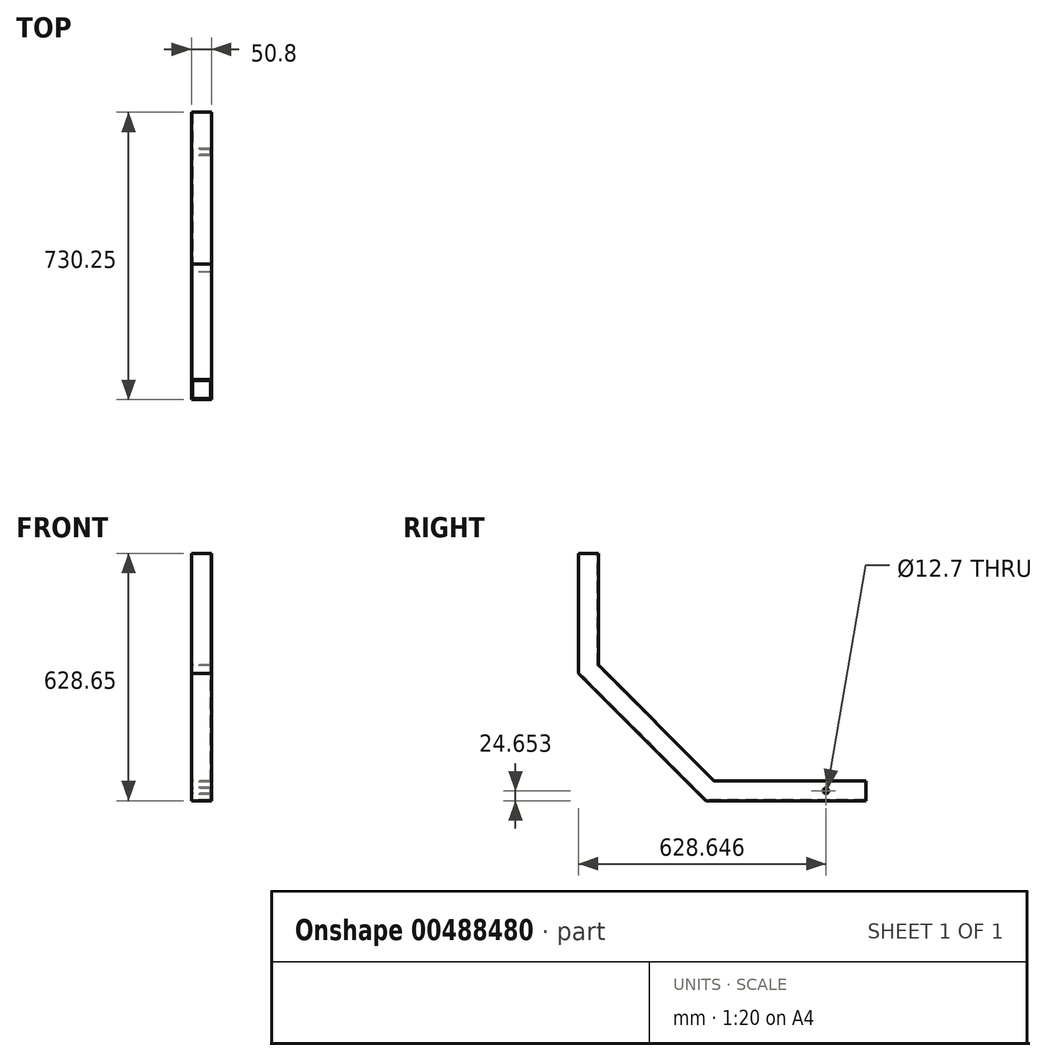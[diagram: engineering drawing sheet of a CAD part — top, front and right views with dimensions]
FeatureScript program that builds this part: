
annotation { "Feature Type Name" : "Feature", "Feature Type Description" : "" }
export const myFeature = defineFeature(function(context is Context, id is Id, definition is map)
    precondition{}
    {
        {
            var Q0;
            Q0=qCreatedBy(makeId("Right.planeOp"),FACE);
            var sketch = newSketch(context, id + "F0", { "sketchPlane" : qUnion([Q0])});
            skLineSegment(sketch, "E0", {"start": v(223.09, -341.59) * mm, "end": v(-183.31, -341.59) * mm});
            skLineSegment(sketch, "E1", {"start": v(-183.31, -341.59) * mm, "end": v(-507.16, -17.74) * mm});
            skLineSegment(sketch, "E2", {"start": v(-507.16, -17.74) * mm, "end": v(-507.16, 287.06) * mm});
            skLineSegment(sketch, "E3", {"start": v(223.09, -341.59) * mm, "end": v(223.09, -290.79) * mm});
            skLineSegment(sketch, "E4", {"start": v(223.09, -290.79) * mm, "end": v(-162.27, -290.79) * mm});
            skLineSegment(sketch, "E5", {"start": v(-162.27, -290.79) * mm, "end": v(-456.36, 3.3) * mm});
            skLineSegment(sketch, "E6", {"start": v(-456.36, 3.3) * mm, "end": v(-456.36, 287.06) * mm});
            skLineSegment(sketch, "E7", {"start": v(-456.36, 287.06) * mm, "end": v(-507.16, 287.06) * mm});
            skCircle(sketch, "E8", {"center": v(121.49, -316.94) * mm, "radius": 6.35 * mm});
            skSolve(sketch);
        }
        {
            var Q0;
            Q0=makeQuery(id+"F0.imprint","IMPRINT",FACE,{"disambiguationData":[TD([[makeQuery(id+"F0.imprint","IMPRINT",EDGE,{"derivedFrom":sQuery(id+"F0.wireOp",EDGE,"E0")}),-1.0]])]});
            extrude(context, id + "F1", {"entities" : qUnion([Q0]), "depth" : 50.8 * mm, "symmetric" : true});
        }
        {
            var Q0;
            Q0=makeQuery(id+"F1.opExtrude","SWEPT_FACE",FACE,{"disambiguationData":[OSD([sQuery(id+"F0.wireOp",EDGE,"E3")])]});
            var Q1;
            Q1=makeQuery(id+"F1.opExtrude","SWEPT_FACE",FACE,{"disambiguationData":[OSD([sQuery(id+"F0.wireOp",EDGE,"E7")])]});
            shell(context, id + "F2", {"entities" : qUnion([Q0, Q1]), "thickness" : 2.54 * mm});
        }
    });
